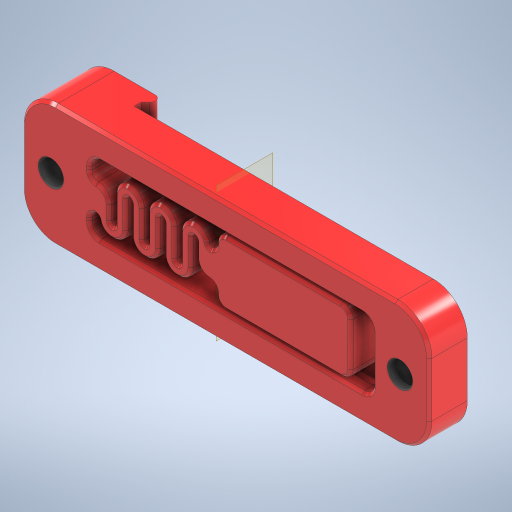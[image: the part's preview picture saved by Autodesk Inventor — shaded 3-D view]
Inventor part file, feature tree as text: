
AUTODESK INVENTOR PART (.ipt)
format: ipt  version: 2023.1 (Build 271208000, 208)  size: 611,328 bytes
history: native  units: mm
features: sketch x4, move_body x4, direct_edit x3, chamfer x3, hole x3, fillet x2, extrude x1, plane x1, delete_face x1
ambient origin geometry x8: Origin, YZ Plane, XZ Plane, XY Plane, X Axis, Y Axis, Z Axis, Center Point
bodies: Volumenkörper2 (feature_tree), Body3 (feature_tree)
feature tree (22):
  direct_edit  "Direktbearbeitung1"
  extrude  "Extrusion1"  Depth=1.0mm
  fillet  "Rundung1"  Radius=1.0mm
  chamfer  "Fase1"  Distance=10.0mm
  fillet  "Rundung2"  Radius=0.8mm
  hole  "Bohrung1"  [1 undecoded]
  chamfer  "Fase2"  Distance=0.4mm
  direct_edit  "Direktbearbeitung2"
  plane  "Arbeitsebene2"
  direct_edit  "Direktbearbeitung3"
  sketch  "Skizze3"  dims[d13=2.86mm d14=6.0mm d15=5.8mm d16=3.0mm d17=90.0deg d18=8.0mm d19=20.594885mm d20=0.4mm d21=2.0mm d22=11.34464mm]
  sketch  "Skizze4"  dims[d23=0.0mm d24=0.0mm d25=3.0mm d26=1.5mm d27=0.0mm d28=0.0mm d29=0.0mm d30=0.0mm d31=1.0mm d32=3.34mm d33=6.0mm d34=4.7mm d35=5.0mm d36=90.0deg d37=8.0mm d38=20.594885mm d39=3.34mm d40=6.0mm d41=4.7mm d42=4.6mm d43=90.0deg d44=8.0mm d45=20.594885mm d46=0.2mm d47=2.0mm d48=45.0deg]
  delete_face  "Fläche löschen1"
  hole  "Bohrung2"  [1 undecoded]
  hole  "Bohrung3"  [1 undecoded]
  chamfer  "Fase3"  Distance=0.2mm Angle=45.0deg
  sketch  "Skizze1"  dims[d0=0.0mm d1=0.0mm d2=1.5mm d3=1.0mm d4=1.0mm d6=10.0mm d7=0.0mm d8=0.8mm]
  sketch  "Skizze2"  dims[d9=0.5mm d10=2.0mm d11=45.0deg d12=0.8mm]
  move_body  "Verschieben1"
  move_body  "Verschieben2"
  move_body  "Verschieben3"
  move_body  "Verschieben4"
note: 3 required parameter values undecoded (feature->parameter linkage not recoverable at this tier; creation-order binding heuristic only, values carry confidence <= 0.55)
